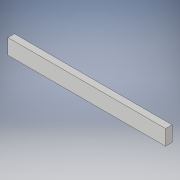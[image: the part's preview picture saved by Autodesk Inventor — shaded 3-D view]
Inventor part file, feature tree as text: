
AUTODESK INVENTOR PART (.ipt)
format: ipt  version: 2017 (Build 210142000, 142)  size: 92,160 bytes
history: native  units: in
note: dims shown in document units (in); Inventor stores cm internally (conversion verified against a paired STEP export)
features: extrude x1, sketch x1
ambient origin geometry x8: Origin, YZ Plane, XZ Plane, XY Plane, X Axis, Y Axis, Z Axis, Center Point
bodies: Solid1 (feature_tree)
feature tree (2):
  extrude  "Extrusion1"  Depth=3.5in
  sketch  "Sketch1"  dims[d0=36.0in d1=3.5in d2=1.5in d3=0.0in]
